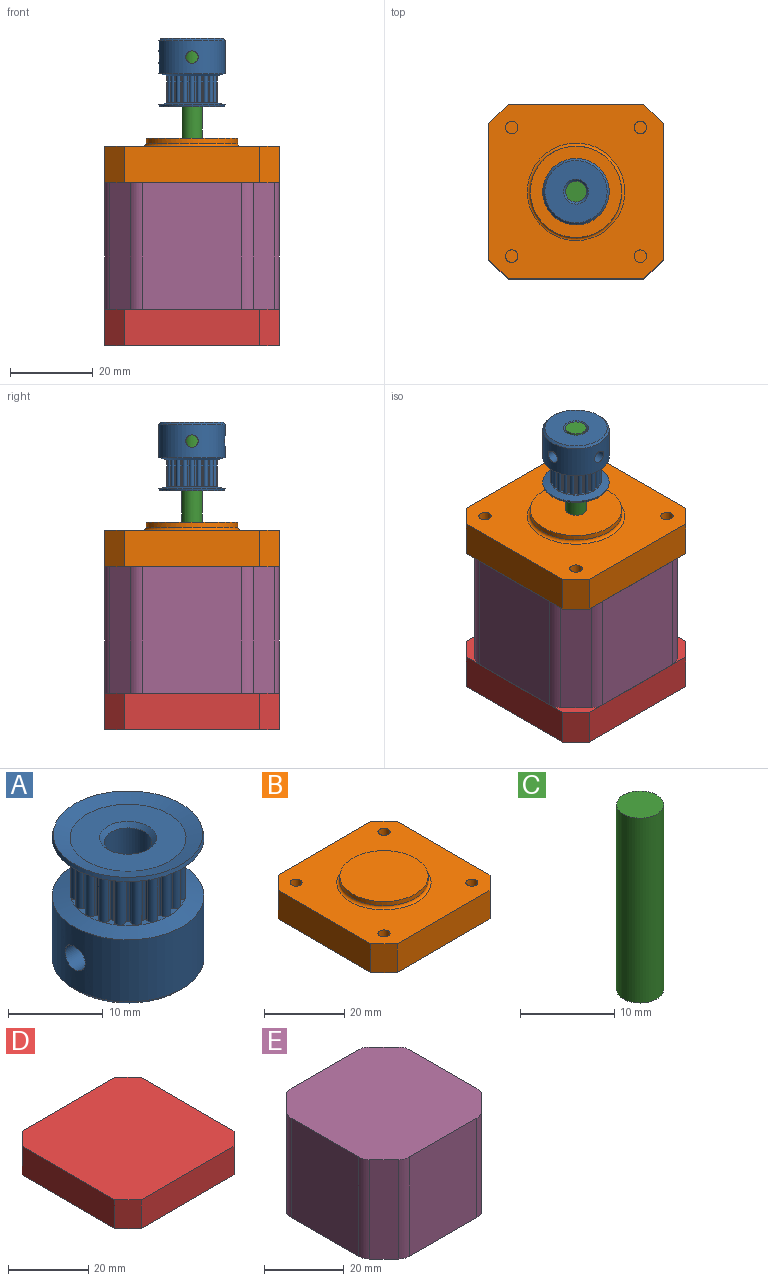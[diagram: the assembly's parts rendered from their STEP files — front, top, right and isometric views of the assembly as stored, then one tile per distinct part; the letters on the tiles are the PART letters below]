
ASSEMBLY  parts=5 mates=4
PART A: 173 faces, bbox 16x16x16.5 mm
  f0: cone r=6.11mm half-angle=75deg, axis (0,0,1), area 86.7mm2, adj f1,f16,f17,f63,f64,f65,f66,f67
  f1: cone r=8mm half-angle=15deg, axis (0,0,-1), area 24.1mm2, adj f0,f2
  f2: cone r=7.88mm half-angle=75deg, axis (0,0,1), area 80.3mm2, adj f1,f3
  f3: plane 12.22x12.22mm, normal (0,0,1), area 89mm2, adj f2,f4
  f4: cone r=3mm half-angle=45deg, axis (0,0,1), area 12.2mm2, adj f3,f5
  f5: cylinder r=2.5mm len=15mm, axis (0,0,1), area 220.7mm2, adj f4,f6,f171,f172
  f6: cone r=2.5mm half-angle=45deg, axis (0,0,-1), area 12.2mm2, adj f5,f7
  f7: plane 15x15mm, normal (0,0,-1), area 148.4mm2, adj f6,f8
  f8: cone r=7.5mm half-angle=45deg, axis (0,0,1), area 34.4mm2, adj f7,f9
  f9: cylinder r=8mm len=16mm, axis (0,0,1), area 387.6mm2, adj f8,f10,f171,f172
  f10: cone r=8mm half-angle=75deg, axis (0,0,-1), area 86.7mm2, adj f9,f14,f15,f45,f46,f47,f48,f49
  f11: plane 6.5x0.02mm, normal (-0.98,0.19,0), area 0.2mm2, adj f14,f16,f18,f43
  f12: cylinder r=0.56mm len=6.5mm, axis (0,0,1), area 11.3mm2, adj f14,f15,f16,f17,f19,f20
  f13: plane 6.5x0.02mm, normal (0.98,0.19,0), area 0.2mm2, adj f15,f17,f21,f44
  f14: plane 1.89x0.85mm, normal (0,0,1), area 0.6mm2, adj f10,f11,f12,f18,f19,f23,f33,f43
  f15: plane 1.89x0.85mm, normal (0,0,1), area 0.6mm2, adj f10,f12,f13,f20,f21,f22,f24,f44
  f16: plane 1.89x0.85mm, normal (0,0,-1), area 0.6mm2, adj f0,f11,f12,f18,f19,f23,f33,f43
  f17: plane 1.89x0.85mm, normal (0,0,-1), area 0.6mm2, adj f0,f12,f13,f20,f21,f22,f24,f44
  f18: cylinder r=5.35mm len=6.5mm, axis (0,0,1), area 2.2mm2, adj f11,f14,f16,f23
  f19: cylinder r=0.27mm len=6.5mm, axis (0,0,1), area 1.7mm2, adj f12,f14,f16,f23
  f20: cylinder r=0.27mm len=6.5mm, axis (0,0,1), area 1.7mm2, adj f12,f15,f17,f22
  f21: cylinder r=5.35mm len=6.5mm, axis (0,0,1), area 2.2mm2, adj f13,f15,f17,f22
  f22: plane 6.5x0.02mm, normal (-0.99,-0.13,0), area 0.2mm2, adj f15,f17,f20,f21
  f23: plane 6.5x0.02mm, normal (0.99,-0.13,0), area 0.2mm2, adj f14,f16,f18,f19
  f24: cylinder r=0.56mm len=6.5mm, axis (0,0,1), area 11.3mm2, adj f15,f17,f44,f62,f80,f81
  f25: cylinder r=0.56mm len=6.5mm, axis (0,0,1), area 11.3mm2, adj f60,f61,f78,f79,f85,f86
  f26: cylinder r=0.56mm len=6.5mm, axis (0,0,1), area 11.3mm2, adj f58,f59,f76,f77,f90,f91
  f27: cylinder r=0.56mm len=6.5mm, axis (0,0,1), area 11.3mm2, adj f56,f57,f74,f75,f95,f96
  f28: cylinder r=0.56mm len=6.5mm, axis (0,0,1), area 11.3mm2, adj f54,f55,f72,f73,f100,f101
  f29: cylinder r=0.56mm len=6.5mm, axis (0,0,1), area 11.3mm2, adj f52,f53,f70,f71,f105,f106
  f30: cylinder r=0.56mm len=6.5mm, axis (0,0,1), area 11.3mm2, adj f50,f51,f68,f69,f110,f111
  f31: cylinder r=0.56mm len=6.5mm, axis (0,0,1), area 11.3mm2, adj f48,f49,f66,f67,f115,f116
  f32: cylinder r=0.56mm len=6.5mm, axis (0,0,1), area 11.3mm2, adj f46,f47,f64,f65,f120,f121
  f33: cylinder r=0.56mm len=6.5mm, axis (0,0,1), area 11.3mm2, adj f14,f16,f43,f45,f63,f125
  f34: cylinder r=0.56mm len=6.5mm, axis (0,0,1), area 11.3mm2, adj f45,f46,f63,f64,f128,f129
  f35: cylinder r=0.56mm len=6.5mm, axis (0,0,1), area 11.3mm2, adj f47,f48,f65,f66,f133,f134
  f36: cylinder r=0.56mm len=6.5mm, axis (0,0,1), area 11.3mm2, adj f49,f50,f67,f68,f138,f139
  f37: cylinder r=0.56mm len=6.5mm, axis (0,0,1), area 11.3mm2, adj f51,f52,f69,f70,f143,f144
  f38: cylinder r=0.56mm len=6.5mm, axis (0,0,1), area 11.3mm2, adj f53,f54,f71,f72,f148,f149
  f39: cylinder r=0.56mm len=6.5mm, axis (0,0,1), area 11.3mm2, adj f55,f56,f73,f74,f153,f154
  f40: cylinder r=0.56mm len=6.5mm, axis (0,0,1), area 11.3mm2, adj f57,f58,f75,f76,f158,f159
  f41: cylinder r=0.56mm len=6.5mm, axis (0,0,1), area 11.3mm2, adj f59,f60,f77,f78,f163,f164
  f42: cylinder r=0.56mm len=6.5mm, axis (0,0,1), area 11.3mm2, adj f61,f62,f79,f80,f168,f169
  f43: cylinder r=0.27mm len=6.5mm, axis (0,0,1), area 1.7mm2, adj f11,f14,f16,f33
  f44: cylinder r=0.27mm len=6.5mm, axis (0,0,1), area 1.7mm2, adj f13,f15,f17,f24
  f45: plane 1.7x1.12mm, normal (0,0,1), area 0.6mm2, adj f10,f33,f34,f124,f125,f126,f127,f128
  f46: plane 1.35x1.35mm, normal (0,0,1), area 0.6mm2, adj f10,f32,f34,f121,f122,f123,f129,f130
  f47: plane 1.7x1.12mm, normal (0,0,1), area 0.6mm2, adj f10,f32,f35,f119,f120,f131,f132,f133
  f48: plane 1.89x0.85mm, normal (0,0,1), area 0.6mm2, adj f10,f31,f35,f116,f117,f118,f134,f135
  f49: plane 1.89x0.85mm, normal (0,0,1), area 0.6mm2, adj f10,f31,f36,f114,f115,f136,f137,f138
  f50: plane 1.7x1.12mm, normal (0,0,1), area 0.6mm2, adj f10,f30,f36,f111,f112,f113,f139,f140
  f51: plane 1.35x1.35mm, normal (0,0,1), area 0.6mm2, adj f10,f30,f37,f109,f110,f141,f142,f143
  f52: plane 1.7x1.12mm, normal (0,0,1), area 0.6mm2, adj f10,f29,f37,f106,f107,f108,f144,f145
  f53: plane 1.89x0.85mm, normal (0,0,1), area 0.6mm2, adj f10,f29,f38,f104,f105,f146,f147,f148
  f54: plane 1.89x0.85mm, normal (0,0,1), area 0.6mm2, adj f10,f28,f38,f101,f102,f103,f149,f150
  f55: plane 1.7x1.12mm, normal (0,0,1), area 0.6mm2, adj f10,f28,f39,f99,f100,f151,f152,f153
  f56: plane 1.35x1.35mm, normal (0,0,1), area 0.6mm2, adj f10,f27,f39,f96,f97,f98,f154,f155
  f57: plane 1.7x1.12mm, normal (0,0,1), area 0.6mm2, adj f10,f27,f40,f94,f95,f156,f157,f158
  f58: plane 1.89x0.85mm, normal (0,0,1), area 0.6mm2, adj f10,f26,f40,f91,f92,f93,f159,f160
  f59: plane 1.89x0.85mm, normal (0,0,1), area 0.6mm2, adj f10,f26,f41,f89,f90,f161,f162,f163
  f60: plane 1.7x1.12mm, normal (0,0,1), area 0.6mm2, adj f10,f25,f41,f86,f87,f88,f164,f165
  f61: plane 1.35x1.35mm, normal (0,0,1), area 0.6mm2, adj f10,f25,f42,f84,f85,f166,f167,f168
  f62: plane 1.7x1.12mm, normal (0,0,1), area 0.6mm2, adj f10,f24,f42,f81,f82,f83,f169,f170
  f63: plane 1.7x1.12mm, normal (0,0,-1), area 0.6mm2, adj f0,f33,f34,f124,f125,f126,f127,f128
  f64: plane 1.35x1.35mm, normal (0,0,-1), area 0.6mm2, adj f0,f32,f34,f121,f122,f123,f129,f130
  f65: plane 1.7x1.12mm, normal (0,0,-1), area 0.6mm2, adj f0,f32,f35,f119,f120,f131,f132,f133
  f66: plane 1.89x0.85mm, normal (0,0,-1), area 0.6mm2, adj f0,f31,f35,f116,f117,f118,f134,f135
  f67: plane 1.89x0.85mm, normal (0,0,-1), area 0.6mm2, adj f0,f31,f36,f114,f115,f136,f137,f138
  f68: plane 1.7x1.12mm, normal (0,0,-1), area 0.6mm2, adj f0,f30,f36,f111,f112,f113,f139,f140
  f69: plane 1.35x1.35mm, normal (0,0,-1), area 0.6mm2, adj f0,f30,f37,f109,f110,f141,f142,f143
  f70: plane 1.7x1.12mm, normal (0,0,-1), area 0.6mm2, adj f0,f29,f37,f106,f107,f108,f144,f145
  f71: plane 1.89x0.85mm, normal (0,0,-1), area 0.6mm2, adj f0,f29,f38,f104,f105,f146,f147,f148
  f72: plane 1.89x0.85mm, normal (0,0,-1), area 0.6mm2, adj f0,f28,f38,f101,f102,f103,f149,f150
  f73: plane 1.7x1.12mm, normal (0,0,-1), area 0.6mm2, adj f0,f28,f39,f99,f100,f151,f152,f153
  f74: plane 1.35x1.35mm, normal (0,0,-1), area 0.6mm2, adj f0,f27,f39,f96,f97,f98,f154,f155
  f75: plane 1.7x1.12mm, normal (0,0,-1), area 0.6mm2, adj f0,f27,f40,f94,f95,f156,f157,f158
  f76: plane 1.89x0.85mm, normal (0,0,-1), area 0.6mm2, adj f0,f26,f40,f91,f92,f93,f159,f160
  f77: plane 1.89x0.85mm, normal (0,0,-1), area 0.6mm2, adj f0,f26,f41,f89,f90,f161,f162,f163
  f78: plane 1.7x1.12mm, normal (0,0,-1), area 0.6mm2, adj f0,f25,f41,f86,f87,f88,f164,f165
  f79: plane 1.35x1.35mm, normal (0,0,-1), area 0.6mm2, adj f0,f25,f42,f84,f85,f166,f167,f168
  f80: plane 1.7x1.12mm, normal (0,0,-1), area 0.6mm2, adj f0,f24,f42,f81,f82,f83,f169,f170
  f81: cylinder r=0.27mm len=6.5mm, axis (0,0,1), area 1.7mm2, adj f24,f62,f80,f170
  f82: cylinder r=5.35mm len=6.5mm, axis (0,0,1), area 2.2mm2, adj f62,f80,f83,f170
  f83: plane 6.5x0.02mm, normal (0.88,0.48,0), area 0.2mm2, adj f62,f80,f82,f169
  f84: plane 6.5x0.02mm, normal (-0.73,-0.68,0), area 0.2mm2, adj f61,f79,f167,f168
  f85: cylinder r=0.27mm len=6.5mm, axis (0,0,1), area 1.7mm2, adj f25,f61,f79,f166
  f86: cylinder r=0.27mm len=6.5mm, axis (0,0,1), area 1.7mm2, adj f25,f60,f78,f165
  f87: cylinder r=5.35mm len=6.5mm, axis (0,0,1), area 2.2mm2, adj f60,f78,f88,f165
  f88: plane 6.5x0.02mm, normal (0.43,0.9,0), area 0.2mm2, adj f60,f78,f87,f164
  f89: plane 6.5x0.02mm, normal (-0.19,-0.98,0), area 0.2mm2, adj f59,f77,f162,f163
  f90: cylinder r=0.27mm len=6.5mm, axis (0,0,1), area 1.7mm2, adj f26,f59,f77,f161
  f91: cylinder r=0.27mm len=6.5mm, axis (0,0,1), area 1.7mm2, adj f26,f58,f76,f160
  f92: cylinder r=5.35mm len=6.5mm, axis (0,0,1), area 2.2mm2, adj f58,f76,f93,f160
  f93: plane 6.5x0.02mm, normal (-0.19,0.98,0), area 0.2mm2, adj f58,f76,f92,f159
  f94: plane 6.5x0.02mm, normal (0.43,-0.9,0), area 0.2mm2, adj f57,f75,f157,f158
  f95: cylinder r=0.27mm len=6.5mm, axis (0,0,1), area 1.7mm2, adj f27,f57,f75,f156
  f96: cylinder r=0.27mm len=6.5mm, axis (0,0,1), area 1.7mm2, adj f27,f56,f74,f155
  f97: cylinder r=5.35mm len=6.5mm, axis (0,0,1), area 2.2mm2, adj f56,f74,f98,f155
  f98: plane 6.5x0.02mm, normal (-0.73,0.68,0), area 0.2mm2, adj f56,f74,f97,f154
  f99: plane 6.5x0.02mm, normal (0.88,-0.48,0), area 0.2mm2, adj f55,f73,f152,f153
  f100: cylinder r=0.27mm len=6.5mm, axis (0,0,1), area 1.7mm2, adj f28,f55,f73,f151
  f101: cylinder r=0.27mm len=6.5mm, axis (0,0,1), area 1.7mm2, adj f28,f54,f72,f150
  f102: cylinder r=5.35mm len=6.5mm, axis (0,0,1), area 2.2mm2, adj f54,f72,f103,f150
  f103: plane 6.5x0.02mm, normal (-0.99,0.13,0), area 0.2mm2, adj f54,f72,f102,f149
  f104: plane 6.5x0.02mm, normal (0.99,0.13,0), area 0.2mm2, adj f53,f71,f147,f148
  f105: cylinder r=0.27mm len=6.5mm, axis (0,0,1), area 1.7mm2, adj f29,f53,f71,f146
  f106: cylinder r=0.27mm len=6.5mm, axis (0,0,1), area 1.7mm2, adj f29,f52,f70,f145
  f107: cylinder r=5.35mm len=6.5mm, axis (0,0,1), area 2.2mm2, adj f52,f70,f108,f145
  f108: plane 6.5x0.02mm, normal (-0.88,-0.48,0), area 0.2mm2, adj f52,f70,f107,f144
  f109: plane 6.5x0.02mm, normal (0.73,0.68,0), area 0.2mm2, adj f51,f69,f142,f143
  f110: cylinder r=0.27mm len=6.5mm, axis (0,0,1), area 1.7mm2, adj f30,f51,f69,f141
  f111: cylinder r=0.27mm len=6.5mm, axis (0,0,1), area 1.7mm2, adj f30,f50,f68,f140
  f112: cylinder r=5.35mm len=6.5mm, axis (0,0,1), area 2.2mm2, adj f50,f68,f113,f140
  f113: plane 6.5x0.02mm, normal (-0.43,-0.9,0), area 0.2mm2, adj f50,f68,f112,f139
  f114: plane 6.5x0.02mm, normal (0.19,0.98,0), area 0.2mm2, adj f49,f67,f137,f138
  f115: cylinder r=0.27mm len=6.5mm, axis (0,0,1), area 1.7mm2, adj f31,f49,f67,f136
  f116: cylinder r=0.27mm len=6.5mm, axis (0,0,1), area 1.7mm2, adj f31,f48,f66,f135
  f117: cylinder r=5.35mm len=6.5mm, axis (0,0,1), area 2.2mm2, adj f48,f66,f118,f135
  f118: plane 6.5x0.02mm, normal (0.19,-0.98,0), area 0.2mm2, adj f48,f66,f117,f134
  f119: plane 6.5x0.02mm, normal (-0.43,0.9,0), area 0.2mm2, adj f47,f65,f132,f133
  f120: cylinder r=0.27mm len=6.5mm, axis (0,0,1), area 1.7mm2, adj f32,f47,f65,f131
  f121: cylinder r=0.27mm len=6.5mm, axis (0,0,1), area 1.7mm2, adj f32,f46,f64,f130
  f122: cylinder r=5.35mm len=6.5mm, axis (0,0,1), area 2.2mm2, adj f46,f64,f123,f130
  f123: plane 6.5x0.02mm, normal (0.73,-0.68,0), area 0.2mm2, adj f46,f64,f122,f129
  f124: plane 6.5x0.02mm, normal (-0.88,0.48,0), area 0.2mm2, adj f45,f63,f127,f128
  f125: cylinder r=0.27mm len=6.5mm, axis (0,0,1), area 1.7mm2, adj f33,f45,f63,f126
  f126: plane 6.5x0.02mm, normal (0.9,-0.43,0), area 0.2mm2, adj f45,f63,f125,f127
  f127: cylinder r=5.35mm len=6.5mm, axis (0,0,1), area 2.2mm2, adj f45,f63,f124,f126
  f128: cylinder r=0.27mm len=6.5mm, axis (0,0,1), area 1.7mm2, adj f34,f45,f63,f124
  f129: cylinder r=0.27mm len=6.5mm, axis (0,0,1), area 1.7mm2, adj f34,f46,f64,f123
  f130: plane 6.5x0.02mm, normal (-0.68,0.73,0), area 0.2mm2, adj f46,f64,f121,f122
  f131: plane 6.5x0.02mm, normal (0.48,-0.88,0), area 0.2mm2, adj f47,f65,f120,f132
  f132: cylinder r=5.35mm len=6.5mm, axis (0,0,1), area 2.2mm2, adj f47,f65,f119,f131
  f133: cylinder r=0.27mm len=6.5mm, axis (0,0,1), area 1.7mm2, adj f35,f47,f65,f119
  f134: cylinder r=0.27mm len=6.5mm, axis (0,0,1), area 1.7mm2, adj f35,f48,f66,f118
  f135: plane 6.5x0.02mm, normal (-0.13,0.99,0), area 0.2mm2, adj f48,f66,f116,f117
  f136: plane 6.5x0.02mm, normal (-0.13,-0.99,0), area 0.2mm2, adj f49,f67,f115,f137
  f137: cylinder r=5.35mm len=6.5mm, axis (0,0,1), area 2.2mm2, adj f49,f67,f114,f136
  f138: cylinder r=0.27mm len=6.5mm, axis (0,0,1), area 1.7mm2, adj f36,f49,f67,f114
  f139: cylinder r=0.27mm len=6.5mm, axis (0,0,1), area 1.7mm2, adj f36,f50,f68,f113
  f140: plane 6.5x0.02mm, normal (0.48,0.88,0), area 0.2mm2, adj f50,f68,f111,f112
  f141: plane 6.5x0.02mm, normal (-0.68,-0.73,0), area 0.2mm2, adj f51,f69,f110,f142
  f142: cylinder r=5.35mm len=6.5mm, axis (0,0,1), area 2.2mm2, adj f51,f69,f109,f141
  f143: cylinder r=0.27mm len=6.5mm, axis (0,0,1), area 1.7mm2, adj f37,f51,f69,f109
  f144: cylinder r=0.27mm len=6.5mm, axis (0,0,1), area 1.7mm2, adj f37,f52,f70,f108
  f145: plane 6.5x0.02mm, normal (0.9,0.43,0), area 0.2mm2, adj f52,f70,f106,f107
  f146: plane 6.5x0.02mm, normal (-0.98,-0.19,0), area 0.2mm2, adj f53,f71,f105,f147
  f147: cylinder r=5.35mm len=6.5mm, axis (0,0,1), area 2.2mm2, adj f53,f71,f104,f146
  f148: cylinder r=0.27mm len=6.5mm, axis (0,0,1), area 1.7mm2, adj f38,f53,f71,f104
  f149: cylinder r=0.27mm len=6.5mm, axis (0,0,1), area 1.7mm2, adj f38,f54,f72,f103
  f150: plane 6.5x0.02mm, normal (0.98,-0.19,0), area 0.2mm2, adj f54,f72,f101,f102
  f151: plane 6.5x0.02mm, normal (-0.9,0.43,0), area 0.2mm2, adj f55,f73,f100,f152
  f152: cylinder r=5.35mm len=6.5mm, axis (0,0,1), area 2.2mm2, adj f55,f73,f99,f151
  f153: cylinder r=0.27mm len=6.5mm, axis (0,0,1), area 1.7mm2, adj f39,f55,f73,f99
  f154: cylinder r=0.27mm len=6.5mm, axis (0,0,1), area 1.7mm2, adj f39,f56,f74,f98
  f155: plane 6.5x0.02mm, normal (0.68,-0.73,0), area 0.2mm2, adj f56,f74,f96,f97
  f156: plane 6.5x0.02mm, normal (-0.48,0.88,0), area 0.2mm2, adj f57,f75,f95,f157
  f157: cylinder r=5.35mm len=6.5mm, axis (0,0,1), area 2.2mm2, adj f57,f75,f94,f156
  f158: cylinder r=0.27mm len=6.5mm, axis (0,0,1), area 1.7mm2, adj f40,f57,f75,f94
  f159: cylinder r=0.27mm len=6.5mm, axis (0,0,1), area 1.7mm2, adj f40,f58,f76,f93
  f160: plane 6.5x0.02mm, normal (0.13,-0.99,0), area 0.2mm2, adj f58,f76,f91,f92
  f161: plane 6.5x0.02mm, normal (0.13,0.99,0), area 0.2mm2, adj f59,f77,f90,f162
  f162: cylinder r=5.35mm len=6.5mm, axis (0,0,1), area 2.2mm2, adj f59,f77,f89,f161
  f163: cylinder r=0.27mm len=6.5mm, axis (0,0,1), area 1.7mm2, adj f41,f59,f77,f89
  f164: cylinder r=0.27mm len=6.5mm, axis (0,0,1), area 1.7mm2, adj f41,f60,f78,f88
  f165: plane 6.5x0.02mm, normal (-0.48,-0.88,0), area 0.2mm2, adj f60,f78,f86,f87
  f166: plane 6.5x0.02mm, normal (0.68,0.73,0), area 0.2mm2, adj f61,f79,f85,f167
  f167: cylinder r=5.35mm len=6.5mm, axis (0,0,1), area 2.2mm2, adj f61,f79,f84,f166
  f168: cylinder r=0.27mm len=6.5mm, axis (0,0,1), area 1.7mm2, adj f42,f61,f79,f84
  f169: cylinder r=0.27mm len=6.5mm, axis (0,0,1), area 1.7mm2, adj f42,f62,f80,f83
  f170: plane 6.5x0.02mm, normal (-0.9,-0.43,0), area 0.2mm2, adj f62,f80,f81,f82
  f171: cylinder r=1.5mm len=6mm, axis (0,1,0), area 53.5mm2, adj f5,f9
  f172: cylinder r=1.5mm len=6mm, axis (-1,0,0), area 53.5mm2, adj f5,f9
PART B: 21 faces, bbox 42x42x10.8 mm
  f0: plane 8.75x4.64mm, normal (0.71,0.71,0), area 57.4mm2, adj f1,f7,f8,f9
  f1: plane 32.73x8.75mm, normal (1,0,0), area 286.4mm2, adj f0,f2,f8,f9
  f2: plane 8.75x4.64mm, normal (0.71,-0.71,0), area 57.4mm2, adj f1,f3,f8,f9
  f3: plane 32.73x8.75mm, normal (0,-1,0), area 286.4mm2, adj f2,f4,f8,f9
  f4: plane 8.75x4.64mm, normal (-0.71,-0.71,0), area 57.4mm2, adj f3,f5,f8,f9
  f5: plane 32.73x8.75mm, normal (-1,0,0), area 286.4mm2, adj f4,f6,f8,f9
  f6: plane 8.75x4.64mm, normal (-0.71,0.71,0), area 57.4mm2, adj f5,f7,f8,f9
  f7: plane 32.73x8.75mm, normal (0,1,0), area 286.4mm2, adj f0,f6,f8,f9
  f8: plane 42x42mm, normal (0,0,-1), area 1721mm2, adj f0,f1,f2,f3,f4,f5,f6,f7
  f9: plane 42x42mm, normal (0,0,1), area 1259mm2, adj f0,f1,f2,f3,f4,f5,f6,f7
  f10: cylinder r=1.5mm len=4.5mm, axis (0,0,1), area 42.4mm2, adj f9,f11
  f11: plane 3x3mm, normal (0,0,1), area 7.1mm2, adj f10
  f12: cylinder r=1.5mm len=4.5mm, axis (0,0,1), area 42.4mm2, adj f9,f13
  f13: plane 3x3mm, normal (0,0,1), area 7.1mm2, adj f12
  f14: cylinder r=1.5mm len=4.5mm, axis (0,0,1), area 42.4mm2, adj f9,f15
  f15: plane 3x3mm, normal (0,0,1), area 7.1mm2, adj f14
  f16: cylinder r=1.5mm len=4.5mm, axis (0,0,1), area 42.4mm2, adj f9,f17
  f17: plane 3x3mm, normal (0,0,1), area 7.1mm2, adj f16
  f18: cylinder r=11mm len=22mm, axis (0,0,-1), area 86.4mm2, adj f19,f20
  f19: plane 22x22mm, normal (0,0,1), area 380.1mm2, adj f18
  f20: torus R=11.75mm, axis (0,0,-1), area 83.4mm2, adj f9,f18
PART C: 3 faces, bbox 5x5x24 mm
  f0: cylinder r=2.5mm len=24mm, axis (0,0,-1), area 377mm2, adj f1,f2
  f1: plane 5x5mm, normal (0,0,1), area 19.6mm2, adj f0
  f2: plane 5x5mm, normal (0,0,-1), area 19.6mm2, adj f0
PART D: 10 faces, bbox 42x42x8.8 mm
  f0: plane 32.73x8.75mm, normal (0,1,0), area 286.4mm2, adj f1,f7,f8,f9
  f1: plane 8.75x4.64mm, normal (0.71,0.71,0), area 57.4mm2, adj f0,f2,f8,f9
  f2: plane 32.73x8.75mm, normal (1,0,0), area 286.4mm2, adj f1,f3,f8,f9
  f3: plane 8.75x4.64mm, normal (0.71,-0.71,0), area 57.4mm2, adj f2,f4,f8,f9
  f4: plane 32.73x8.75mm, normal (0,-1,0), area 286.4mm2, adj f3,f5,f8,f9
  f5: plane 8.75x4.64mm, normal (-0.71,-0.71,0), area 57.4mm2, adj f4,f6,f8,f9
  f6: plane 32.73x8.75mm, normal (-1,0,0), area 286.4mm2, adj f5,f7,f8,f9
  f7: plane 8.75x4.64mm, normal (-0.71,0.71,0), area 57.4mm2, adj f0,f6,f8,f9
  f8: plane 42x42mm, normal (0,0,-1), area 1721mm2, adj f0,f1,f2,f3,f4,f5,f6,f7
  f9: plane 42x42mm, normal (0,0,1), area 1721mm2, adj f0,f1,f2,f3,f4,f5,f6,f7
PART E: 18 faces, bbox 42x42x30.5 mm
  f0: cylinder r=4mm len=30.5mm, axis (0,0,1), area 95.8mm2, adj f1,f15,f16,f17
  f1: plane 30.5x5.12mm, normal (0.71,-0.71,0), area 220.9mm2, adj f0,f2,f16,f17
  f2: cylinder r=4mm len=30.5mm, axis (0,0,1), area 95.8mm2, adj f1,f3,f16,f17
  f3: plane 30.5x23.76mm, normal (0,-1,0), area 724.6mm2, adj f2,f4,f16,f17
  f4: cylinder r=4mm len=30.5mm, axis (0,0,1), area 95.8mm2, adj f3,f5,f16,f17
  f5: plane 30.5x5.12mm, normal (-0.71,-0.71,0), area 220.9mm2, adj f4,f6,f16,f17
  f6: cylinder r=4mm len=30.5mm, axis (0,0,1), area 95.8mm2, adj f5,f7,f16,f17
  f7: plane 30.5x23.76mm, normal (-1,0,0), area 724.6mm2, adj f6,f8,f16,f17
  f8: cylinder r=4mm len=30.5mm, axis (0,0,1), area 95.8mm2, adj f7,f9,f16,f17
  f9: plane 30.5x5.12mm, normal (-0.71,0.71,0), area 220.9mm2, adj f8,f10,f16,f17
  f10: cylinder r=4mm len=30.5mm, axis (0,0,1), area 95.8mm2, adj f9,f11,f16,f17
  f11: plane 30.5x23.76mm, normal (0,1,0), area 724.6mm2, adj f10,f12,f16,f17
  f12: cylinder r=4mm len=30.5mm, axis (0,0,1), area 95.8mm2, adj f11,f13,f16,f17
  f13: plane 30.5x5.12mm, normal (0.71,0.71,0), area 220.9mm2, adj f12,f14,f16,f17
  f14: cylinder r=4mm len=30.5mm, axis (0,0,1), area 95.8mm2, adj f13,f15,f16,f17
  f15: plane 30.5x23.76mm, normal (1,0,0), area 724.6mm2, adj f0,f14,f16,f17
  f16: plane 42x42mm, normal (0,0,-1), area 1649.8mm2, adj f0,f1,f2,f3,f4,f5,f6,f7
  f17: plane 42x42mm, normal (0,0,1), area 1649.8mm2, adj f0,f1,f2,f3,f4,f5,f6,f7
PLACE A rot(axis=(1,0,0),180deg) t=(37.57,19.22,33.79)mm
PLACE B t=(37.57,19.22,20.29)mm
PLACE C rot(axis=(1,0,0),180deg) t=(37.57,19.22,46.29)mm
PLACE D t=(37.57,19.22,20.29)mm
PLACE E t=(37.57,19.22,20.29)mm
MATE fastened D.f9 <-> E.f16  axis (0,0,1) through (37.57,19.22,-18.96)mm
MATE cylindrical C.f0 <-> B.f18  axis (0,0,-1) through (37.57,19.22,22.29)mm
MATE revolute A.f0 <-> C.f0  axis (0,0,1) through (37.57,19.22,46.29)mm
MATE fastened B.f18 <-> E.f17  axis (0,0,-1) through (37.57,19.22,11.54)mm
